# Revit family: STC_A3-Wood-Bowstring-Truss-inst-param
name_source: partatom
category: Structural Framing
revit_build: Autodesk Revit 2016 (Build: 20150220_1215(x64)
units: mm (PartAtom-declared; Revit-internal decimal feet)

## family parameters
Always export as geometry = No
Always vertical = Yes
Cut with Voids When Loaded = No
Material for Model Behavior = Other
Section Shape = Not Defined
Shared = No
Show family pre-cut in plan views = Yes
Work Plane-Based = No

## types (6) — shared parameters
SeatPlateRadius = 76 mm

## per-type parameters (varying)
| type | BotChordDepth | ChordWidth | PinRadius | SeatPlateThickness | SeatPlateWidth | SpringPtHeight | TopChordDepth | TopChordRadius | WebDim |
| 30' long - 6" x 2" chords | 152 mm | 51 mm | 13 mm | 13 mm | 305 mm | 203 mm | 152 mm | 9144 mm  [stored 30 ft] | 25 mm  [stored 0.082021 ft] |
| 50' long - 9" x 3" chords | 229 mm | 76 mm | 19 mm | 25 mm  [stored 0.082021 ft] | 457 mm | 305 mm | 229 mm | 15240 mm  [stored 50 ft] | 25 mm  [stored 0.082021 ft] |
| 80' long - 12" x 4" chords | 305 mm | 102 mm | 25 mm  [stored 0.082021 ft] | 51 mm | 610 mm | 305 mm | 305 mm | 24384 mm  [stored 80 ft] | 51 mm |
| 100' long - 12" x 43" chords | 305 mm | 102 mm | 25 mm  [stored 0.082021 ft] | 51 mm | 610 mm | 305 mm | 305 mm | 30480 mm  [stored 100 ft] | 51 mm |
| 20' long - 4" x 1" chords | 102 mm | 25 mm  [stored 0.082021 ft] | 13 mm | 13 mm | 305 mm | 152 mm | 102 mm | 6096 mm  [stored 20 ft] | 25 mm  [stored 0.082021 ft] |
| 15' long - 3" x 1" chords | 76 mm | 25 mm  [stored 0.082021 ft] | 6 mm | 13 mm | 305 mm | 152 mm | 76 mm | 4572 mm  [stored 15 ft] | 13 mm |

note: [stored X ft] marks values corroborated as IEEE doubles in the binary element streams (Revit-internal decimal feet)

## geometry (parser evidence)
native form markers: Sweep x1
no freeform markers — native parametric forms only
